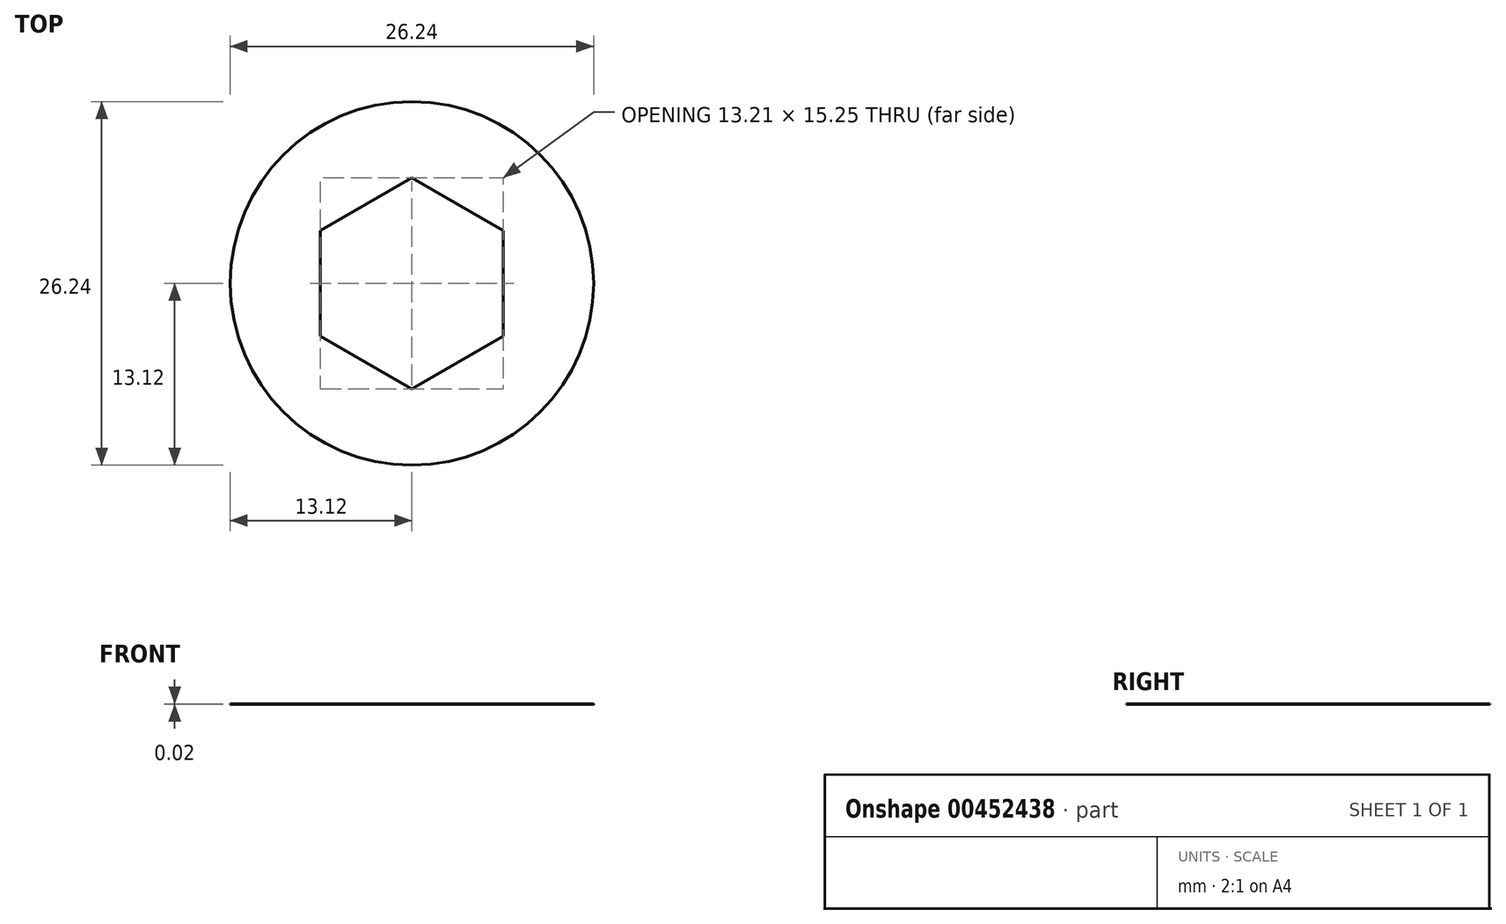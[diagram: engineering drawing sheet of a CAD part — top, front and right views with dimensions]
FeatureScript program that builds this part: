
annotation { "Feature Type Name" : "Feature", "Feature Type Description" : "" }
export const myFeature = defineFeature(function(context is Context, id is Id, definition is map)
    precondition{}
    {
        {
            var Q0;
            Q0=qCreatedBy(makeId("Top.planeOp"),FACE);
            var sketch = newSketch(context, id + "F0", { "sketchPlane" : qUnion([Q0])});
            skCircle(sketch, "E0", {"center": v(0, 0) * mm, "radius": 13.12 * mm});
            skSolve(sketch);
        }
        {
            var Q0;
            Q0=makeQuery(id+"F0.imprint","IMPRINT",FACE,{"disambiguationData":[TD([[makeQuery(id+"F0.imprint","IMPRINT",EDGE,{"derivedFrom":sQuery(id+"F0.wireOp",EDGE,"E0")}),1.0]])]});
            extrude(context, id + "F1", {"entities" : qUnion([Q0]), "depth" : 1 / 50.8 * mm});
        }
        {
            var Q0;
            Q0=qCreatedBy(makeId("Top.planeOp"),FACE);
            var sketch = newSketch(context, id + "F2", { "sketchPlane" : qUnion([Q0])});
            skCircle(sketch, "E1.cCircle", {"center": v(0, 0) * mm, "radius": 6.6 * mm, "construction": true});
            skLineSegment(sketch, "E1.0", {"start": v(6.6, 3.81) * mm, "end": v(6.6, -3.81) * mm});
            skLineSegment(sketch, "E1.1", {"start": v(6.6, -3.81) * mm, "end": v(0, -7.63) * mm});
            skLineSegment(sketch, "E1.2", {"start": v(0, -7.63) * mm, "end": v(-6.6, -3.81) * mm});
            skLineSegment(sketch, "E1.3", {"start": v(-6.6, -3.81) * mm, "end": v(-6.6, 3.81) * mm});
            skLineSegment(sketch, "E1.4", {"start": v(-6.6, 3.81) * mm, "end": v(0, 7.63) * mm});
            skLineSegment(sketch, "E1.5", {"start": v(0, 7.63) * mm, "end": v(6.6, 3.81) * mm});
            skPoint(sketch, "E1.0.midPoint", {"position": v(6.6, 0) * mm});
            skSolve(sketch);
        }
        {
            var Q0;
            Q0=makeQuery(id+"F2.imprint","IMPRINT",FACE,{"disambiguationData":[TD([[makeQuery(id+"F2.imprint","IMPRINT",EDGE,{"derivedFrom":sQuery(id+"F2.wireOp",EDGE,"E1.0")}),-1.0]])]});
            extrude(context, id + "F3", {"entities" : qUnion([Q0]), "operationType" : NewBodyOperationType.REMOVE, "depth" : 36.32 * mm});
        }
    });
